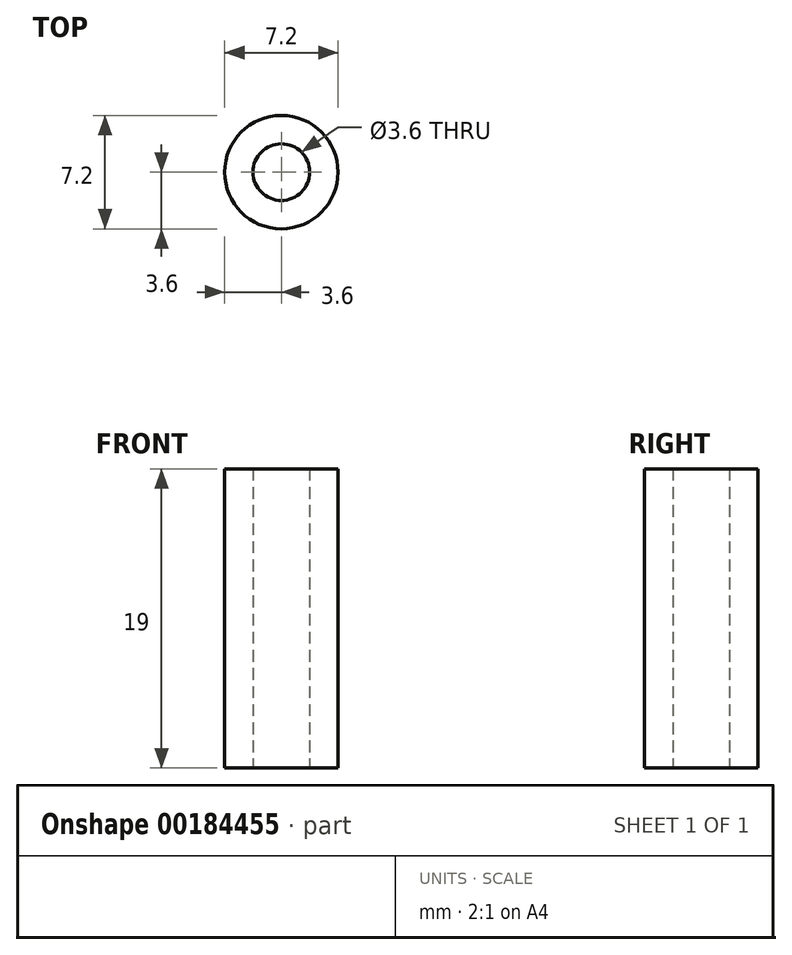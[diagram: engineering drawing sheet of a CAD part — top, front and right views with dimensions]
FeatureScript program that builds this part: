
annotation { "Feature Type Name" : "Feature", "Feature Type Description" : "" }
export const myFeature = defineFeature(function(context is Context, id is Id, definition is map)
    precondition{}
    {
        {
            var Q0;
            Q0=qCreatedBy(makeId("Top.planeOp"),FACE);
            var sketch = newSketch(context, id + "F0", { "sketchPlane" : qUnion([Q0])});
            skCircle(sketch, "E0", {"center": v(0, 0) * mm, "radius": 3.6 * mm});
            skCircle(sketch, "E1", {"center": v(0, 0) * mm, "radius": 1.8 * mm});
            skSolve(sketch);
        }
        {
            var Q0;
            Q0=makeQuery(id+"F0.imprint","IMPRINT",FACE,{"disambiguationData":[TD([[makeQuery(id+"F0.imprint","IMPRINT",EDGE,{"derivedFrom":sQuery(id+"F0.wireOp",EDGE,"E0")}),1.0]])]});
            extrude(context, id + "F1", {"entities" : qUnion([Q0]), "depth" : (12 + 7) * mm});
        }
    });
